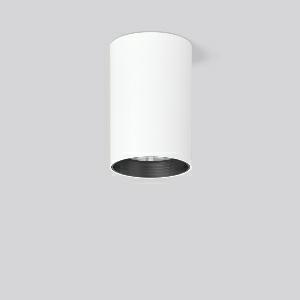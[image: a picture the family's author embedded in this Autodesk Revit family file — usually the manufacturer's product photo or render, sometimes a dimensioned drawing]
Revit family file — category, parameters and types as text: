
# Revit family: heledon_maxi_a_931228_002_1_76_da77
name_source: partatom
category: Lighting Fixtures
units: mm (PartAtom-declared; Revit-internal decimal feet)

## family parameters
Cut with Voids When Loaded = No
Host = Face
Light Source = No
Part Type = Normal
Room Calculation Point = No
Round Connector Dimension = Use Diameter
Shared = No

## types (1)
- HELEDON maxi A (1 x LED Modul 940, 3750 lm, 4000)
    Apparent Load = 35 VA
    Approval mark = CE
    CIE Flux Codes = 96 100 100 100 100
    Color Rendering = 92
    Color Temperature = 4000
    Default Elevation = 1800 mm
    Description = Series: HELEDON maxi
Cylindrical surface-mounted downlight. Housing: die-cast aluminium, powder-coated. Internal ceiling frame polycarbonate with bayonet mounting. Black plastic ring and recessed LED to prevent glare from the side. Optical assembly with lens made of plastic (polycarbonate) for the best homogeneous light distribution - can be changed without tools. Best colour rendering index Ra>90. Suitable for Ceiling mounting. Easy installation with a separate ceiling frame with bayonet mounting and plug connection. Driver integrated. Connected via plug-in connector. High quality converter without flickering and stroboscopic effect. The following accessories can be mounted without use of tools: interchangeable lenses, decorative glasses, honeycomb louvre, clear and frosted diffusers, white interchangeable plastic ring. 
Colour: traffic white, matt (RAL 9016)
Diameter: 123 mm
Height: 183 mm
Lamp: LED
Socket: without socket
Colour temperature: 4000K
Colour rendering index (CRI): 92
System power: 35 W
Rated luminous flux: 3750 lm
Luminous efficiency: 107 lm/W
Control gear: Converter, dimmable, DALI
Protection class: I
Type of protection: IP 20
    Height = 183 mm
    Lamp = 1 x LED Modul 940
    Lamp Light Flux = 3750 lm
    Lamp count = 1
    Length = 123 mm
    Lifetime = 50000 h
    Luminous efficacy = 107 lm/W
    Manufacturer = RZB
    ModVariant = No
    Model = 931228.002.1.76
    Mounting Place = Ceiling
    Mounting Type = Surface mounted
    Number of Poles = 1
    OnlyDefault = Yes
    Power Factor = 1
    Product Name = HELEDON maxi A
    Product group = Surface mounted downlights
    ProductGroupID = 302
    Protection Class = Protection class I
    Protection Degree = IP 20
    RLX_Detail_Level = 1
    RLX_Emergency_Light_Flux = 0 lm
    RLX_Emergency_Type = 0
    RLX_Emergency_Type_DB = No
    RlxData = <blob elided: 96853 chars, md5=6720bffa>
    Socket = socket
    Standby Power = 0 W
    System Light Flux = 3750 lm
    System Power = 35 W
    Type Comments = Product without accessories
    Type Image = 931193.002.jpg
    URL = http://relux.com
    VarID = ---
    Voltage = 230 V
    Voltage Range = 220-240 V
    Weight = 0.00 kg
    Width = 0 mm  [stored 0 ft]

note: [stored X ft] marks values corroborated as IEEE doubles in the binary element streams (Revit-internal decimal feet)

## geometry (parser evidence)
native form markers: Blend x4, Sweep x10
no freeform markers — native parametric forms only
